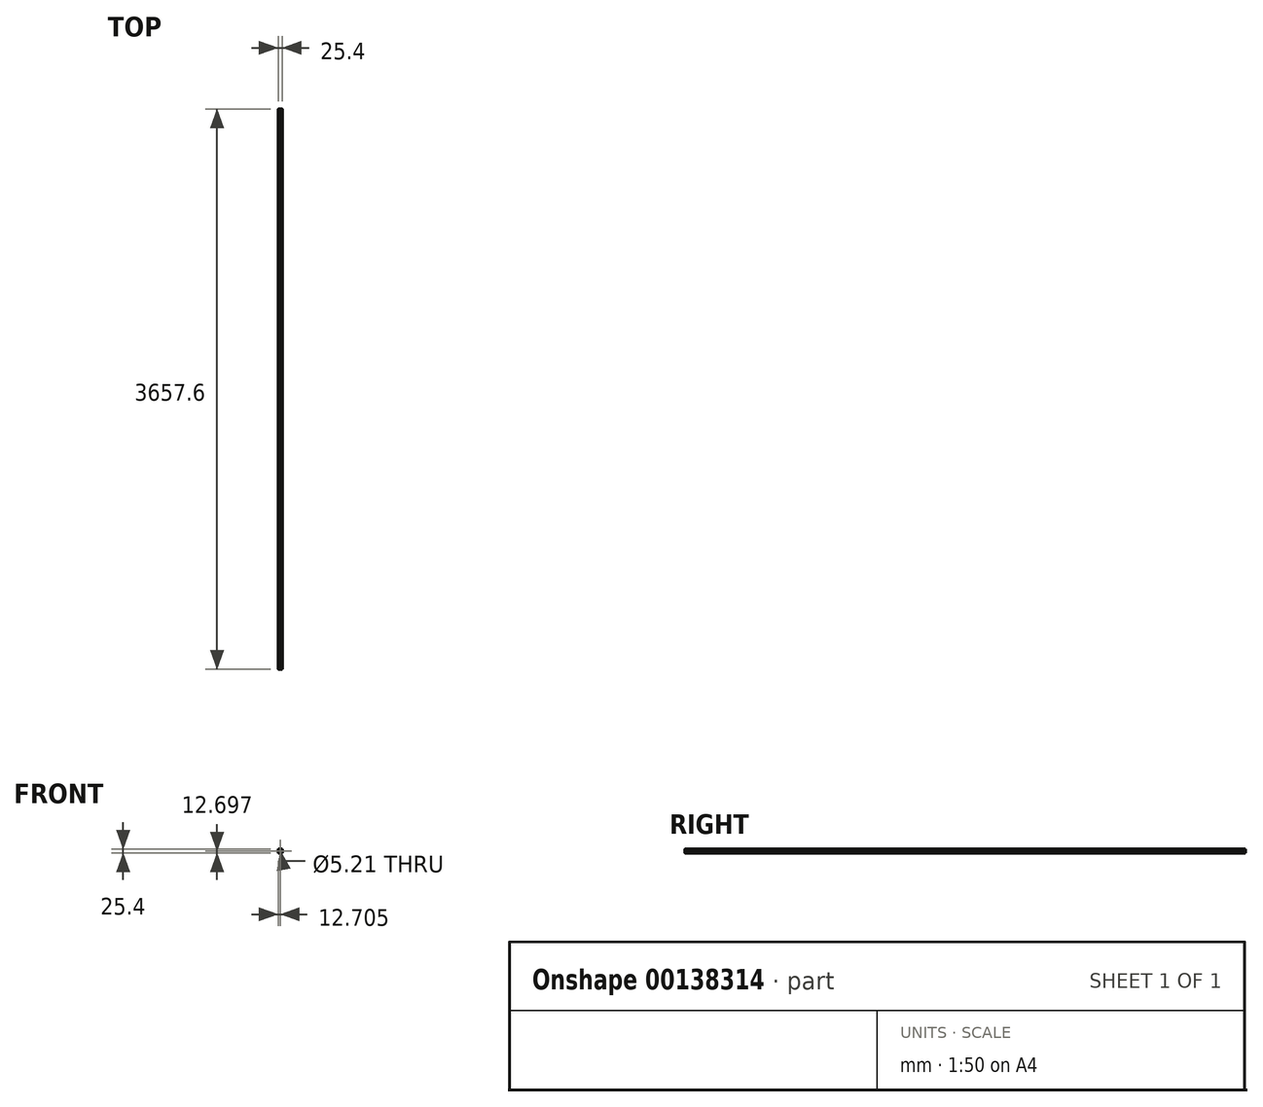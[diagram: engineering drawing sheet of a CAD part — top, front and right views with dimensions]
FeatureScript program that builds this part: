
annotation { "Feature Type Name" : "Feature", "Feature Type Description" : "" }
export const myFeature = defineFeature(function(context is Context, id is Id, definition is map)
    precondition{}
    {
        {
            var Q0;
            Q0=qCreatedBy(makeId("Front.planeOp"),FACE);
            var sketch = newSketch(context, id + "F0", { "sketchPlane" : qUnion([Q0])});
            skLineSegment(sketch, "E0.bottom", {"start": v(-12.7, 12.7) * mm, "end": v(12.7, 12.7) * mm});
            skLineSegment(sketch, "E0.top", {"start": v(-12.7, -12.7) * mm, "end": v(12.7, -12.7) * mm});
            skLineSegment(sketch, "E0.left", {"start": v(-12.7, 12.7) * mm, "end": v(-12.7, -12.7) * mm});
            skLineSegment(sketch, "E0.right", {"start": v(12.7, 12.7) * mm, "end": v(12.7, -12.7) * mm});
            skPoint(sketch, "E0.middle", {"position": v(0, 0) * mm});
            skLineSegment(sketch, "E1.bottom", {"start": v(-0.33, 4.52) * mm, "end": v(0.33, 4.52) * mm});
            skLineSegment(sketch, "E1.right", {"start": v(4.52, 3.37) * mm, "end": v(4.52, -2.64) * mm});
            skCircle(sketch, "E2", {"center": v(0, 0) * mm, "radius": 2.6 * mm});
            skLineSegment(sketch, "E3.0", {"start": v(-0.87, 4.74) * mm, "end": v(-7.97, 11.84) * mm});
            skLineSegment(sketch, "E4.0", {"start": v(-5.3, 3.74) * mm, "end": v(-13.48, 11.92) * mm});
            skLineSegment(sketch, "E5.MirrorCS", {"start": v(0.87, 4.74) * mm, "end": v(7.97, 11.84) * mm});
            skLineSegment(sketch, "E6.MirrorCS", {"start": v(5.3, 3.74) * mm, "end": v(13.48, 11.92) * mm});
            skLineSegment(sketch, "E7.MirrorCS", {"start": v(-4.64, 3.08) * mm, "end": v(-13.48, 11.92) * mm});
            skLineSegment(sketch, "E8.MirrorCS", {"start": v(-4.74, -3.18) * mm, "end": v(-13.48, -11.92) * mm});
            skLineSegment(sketch, "E9.MirrorCS", {"start": v(-5.3, -3.74) * mm, "end": v(-13.48, -11.92) * mm});
            skLineSegment(sketch, "E10.MirrorCS", {"start": v(-0.87, -4.74) * mm, "end": v(-7.97, -11.84) * mm});
            skLineSegment(sketch, "E11.MirrorCS", {"start": v(0.64, -4.52) * mm, "end": v(7.97, -11.84) * mm});
            skLineSegment(sketch, "E12.MirrorCS", {"start": v(0.87, -4.74) * mm, "end": v(7.97, -11.84) * mm});
            skLineSegment(sketch, "E13.MirrorCS", {"start": v(4.74, -3.18) * mm, "end": v(13.48, -11.92) * mm});
            skPoint(sketch, "E14.orphan", {"position": v(-5.3, 3.74) * mm});
            skPoint(sketch, "E15.orphan", {"position": v(-5.3, -3.74) * mm});
            skArc(sketch, "E16.filletArc", {"start": v(-0.33, -4.52) * mm, "mid": v(-0.62, -4.58) * mm, "end": v(-0.87, -4.74) * mm});
            skArc(sketch, "E17.filletArc", {"start": v(-4.74, -3.18) * mm, "mid": v(-4.58, -2.93) * mm, "end": v(-4.52, -2.64) * mm});
            skLineSegment(sketch, "E18", {"start": v(-4.52, -2.64) * mm, "end": v(-4.52, 2.41) * mm});
            skArc(sketch, "E19.filletArc", {"start": v(-0.87, 4.74) * mm, "mid": v(-0.62, 4.58) * mm, "end": v(-0.33, 4.52) * mm});
            skArc(sketch, "E20.filletArc", {"start": v(0.33, 4.52) * mm, "mid": v(0.62, 4.58) * mm, "end": v(0.87, 4.74) * mm});
            skArc(sketch, "E21.filletArc", {"start": v(4.52, -2.64) * mm, "mid": v(4.58, -2.93) * mm, "end": v(4.74, -3.18) * mm});
            skLineSegment(sketch, "E22", {"start": v(-0.33, -4.52) * mm, "end": v(0.33, -4.52) * mm});
            skPoint(sketch, "E23.visualSharp", {"position": v(0.64, -4.52) * mm});
            skArc(sketch, "E23.filletArc", {"start": v(0.87, -4.74) * mm, "mid": v(0.62, -4.58) * mm, "end": v(0.33, -4.52) * mm});
            skArc(sketch, "E24", {"start": v(-120.05, 65.1) * mm, "mid": v(-119.54, 65.6) * mm, "end": v(-120.05, 66.12) * mm});
            skLineSegment(sketch, "E25", {"start": v(-120.05, 69.33) * mm, "end": v(-120.05, 66.12) * mm});
            skArc(sketch, "E26", {"start": v(-120.05, 69.33) * mm, "mid": v(-119.54, 69.84) * mm, "end": v(-120.05, 70.35) * mm});
            skLineSegment(sketch, "E27", {"start": v(-120.05, 71.32) * mm, "end": v(-120.05, 70.35) * mm});
            skArc(sketch, "E28", {"start": v(-117.84, 71.32) * mm, "mid": v(-118.94, 72.43) * mm, "end": v(-120.05, 71.32) * mm});
            skLineSegment(sketch, "E29", {"start": v(-117.84, 69.2) * mm, "end": v(-117.84, 71.32) * mm});
            skArc(sketch, "E30", {"start": v(-117.84, 69.2) * mm, "mid": v(-117.2, 68.25) * mm, "end": v(-116.1, 68.47) * mm});
            skLineSegment(sketch, "E31", {"start": v(-112.77, 71.8) * mm, "end": v(-116.1, 68.47) * mm});
            skArc(sketch, "E32", {"start": v(-112.77, 71.8) * mm, "mid": v(-112.08, 72.83) * mm, "end": v(-111.84, 74.05) * mm});
            skLineSegment(sketch, "E33", {"start": v(-111.84, 77.28) * mm, "end": v(-111.84, 74.05) * mm});
            skArc(sketch, "E34", {"start": v(-111.84, 77.28) * mm, "mid": v(-112.08, 78.5) * mm, "end": v(-112.77, 79.53) * mm});
            skLineSegment(sketch, "E35", {"start": v(-116.1, 82.86) * mm, "end": v(-112.77, 79.53) * mm});
            skArc(sketch, "E36", {"start": v(-116.1, 82.86) * mm, "mid": v(-117.2, 83.08) * mm, "end": v(-117.84, 82.14) * mm});
            skLineSegment(sketch, "E37", {"start": v(-117.84, 80.01) * mm, "end": v(-117.84, 82.14) * mm});
            skArc(sketch, "E38", {"start": v(-120.05, 80.01) * mm, "mid": v(-118.94, 78.9) * mm, "end": v(-117.84, 80.01) * mm});
            skLineSegment(sketch, "E39", {"start": v(-120.05, 80.98) * mm, "end": v(-120.05, 80.01) * mm});
            skArc(sketch, "E40", {"start": v(-120.05, 80.98) * mm, "mid": v(-119.54, 81.5) * mm, "end": v(-120.05, 82) * mm});
            skLineSegment(sketch, "E41", {"start": v(-120.05, 85.22) * mm, "end": v(-120.05, 82) * mm});
            skArc(sketch, "E42", {"start": v(-120.05, 85.22) * mm, "mid": v(-119.54, 85.72) * mm, "end": v(-120.05, 86.23) * mm});
            skArc(sketch, "E43", {"start": v(-117.91, 88.37) * mm, "mid": v(-119.43, 87.75) * mm, "end": v(-120.05, 86.23) * mm});
            skArc(sketch, "E44", {"start": v(-117.91, 88.37) * mm, "mid": v(-117.4, 87.86) * mm, "end": v(-116.9, 88.37) * mm});
            skLineSegment(sketch, "E45", {"start": v(-113.68, 88.37) * mm, "end": v(-116.9, 88.37) * mm});
            skArc(sketch, "E46", {"start": v(-113.68, 88.37) * mm, "mid": v(-113.17, 87.86) * mm, "end": v(-112.66, 88.37) * mm});
            skLineSegment(sketch, "E47", {"start": v(-111.69, 88.37) * mm, "end": v(-112.66, 88.37) * mm});
            skArc(sketch, "E48", {"start": v(-111.69, 86.16) * mm, "mid": v(-110.58, 87.26) * mm, "end": v(-111.69, 88.37) * mm});
            skLineSegment(sketch, "E49", {"start": v(-113.82, 86.16) * mm, "end": v(-111.69, 86.16) * mm});
            skArc(sketch, "E50", {"start": v(-113.82, 86.16) * mm, "mid": v(-114.76, 85.53) * mm, "end": v(-114.54, 84.42) * mm});
            skLineSegment(sketch, "E51", {"start": v(-111.2, 81.1) * mm, "end": v(-114.54, 84.42) * mm});
            skArc(sketch, "E52", {"start": v(-111.2, 81.1) * mm, "mid": v(-110.18, 80.4) * mm, "end": v(-108.96, 80.16) * mm});
            skLineSegment(sketch, "E53", {"start": v(-105.73, 80.16) * mm, "end": v(-108.96, 80.16) * mm});
            skArc(sketch, "E54", {"start": v(-105.73, 80.16) * mm, "mid": v(-104.51, 80.4) * mm, "end": v(-103.48, 81.1) * mm});
            skLineSegment(sketch, "E55", {"start": v(-100.15, 84.42) * mm, "end": v(-103.48, 81.1) * mm});
            skArc(sketch, "E56", {"start": v(-100.15, 84.42) * mm, "mid": v(-99.93, 85.53) * mm, "end": v(-100.87, 86.16) * mm});
            skLineSegment(sketch, "E57", {"start": v(-103, 86.16) * mm, "end": v(-100.87, 86.16) * mm});
            skArc(sketch, "E58", {"start": v(-103, 88.37) * mm, "mid": v(-104.1, 87.26) * mm, "end": v(-103, 86.16) * mm});
            skLineSegment(sketch, "E59", {"start": v(-102.03, 88.37) * mm, "end": v(-103, 88.37) * mm});
            skArc(sketch, "E60", {"start": v(-102.03, 88.37) * mm, "mid": v(-101.52, 87.86) * mm, "end": v(-101.01, 88.37) * mm});
            skLineSegment(sketch, "E61", {"start": v(-97.8, 88.37) * mm, "end": v(-101.01, 88.37) * mm});
            skArc(sketch, "E62", {"start": v(-97.8, 88.37) * mm, "mid": v(-97.29, 87.86) * mm, "end": v(-96.78, 88.37) * mm});
            skArc(sketch, "E63", {"start": v(-94.65, 86.23) * mm, "mid": v(-95.26, 87.75) * mm, "end": v(-96.78, 88.37) * mm});
            skArc(sketch, "E64", {"start": v(-94.65, 86.23) * mm, "mid": v(-95.15, 85.72) * mm, "end": v(-94.65, 85.22) * mm});
            skLineSegment(sketch, "E65", {"start": v(-94.65, 82) * mm, "end": v(-94.65, 85.22) * mm});
            skArc(sketch, "E66", {"start": v(-94.65, 82) * mm, "mid": v(-95.15, 81.5) * mm, "end": v(-94.65, 80.98) * mm});
            skLineSegment(sketch, "E67", {"start": v(-94.65, 80.01) * mm, "end": v(-94.65, 80.98) * mm});
            skArc(sketch, "E68", {"start": v(-96.86, 80.01) * mm, "mid": v(-95.75, 78.9) * mm, "end": v(-94.65, 80.01) * mm});
            skLineSegment(sketch, "E69", {"start": v(-96.86, 82.14) * mm, "end": v(-96.86, 80.01) * mm});
            skArc(sketch, "E70", {"start": v(-96.86, 82.14) * mm, "mid": v(-97.48, 83.08) * mm, "end": v(-98.59, 82.86) * mm});
            skLineSegment(sketch, "E71", {"start": v(-101.92, 79.53) * mm, "end": v(-98.59, 82.86) * mm});
            skArc(sketch, "E72", {"start": v(-101.92, 79.53) * mm, "mid": v(-102.6, 78.5) * mm, "end": v(-102.85, 77.28) * mm});
            skLineSegment(sketch, "E73", {"start": v(-102.85, 74.05) * mm, "end": v(-102.85, 77.28) * mm});
            skArc(sketch, "E74", {"start": v(-102.85, 74.05) * mm, "mid": v(-102.6, 72.83) * mm, "end": v(-101.92, 71.8) * mm});
            skLineSegment(sketch, "E75", {"start": v(-98.59, 68.47) * mm, "end": v(-101.92, 71.8) * mm});
            skArc(sketch, "E76", {"start": v(-98.59, 68.47) * mm, "mid": v(-97.48, 68.25) * mm, "end": v(-96.86, 69.2) * mm});
            skLineSegment(sketch, "E77", {"start": v(-96.86, 71.32) * mm, "end": v(-96.86, 69.2) * mm});
            skArc(sketch, "E78", {"start": v(-94.65, 71.32) * mm, "mid": v(-95.75, 72.43) * mm, "end": v(-96.86, 71.32) * mm});
            skLineSegment(sketch, "E79", {"start": v(-94.65, 70.35) * mm, "end": v(-94.65, 71.32) * mm});
            skArc(sketch, "E80", {"start": v(-94.65, 70.35) * mm, "mid": v(-95.15, 69.84) * mm, "end": v(-94.65, 69.33) * mm});
            skLineSegment(sketch, "E81", {"start": v(-94.65, 66.12) * mm, "end": v(-94.65, 69.33) * mm});
            skArc(sketch, "E82", {"start": v(-94.65, 66.12) * mm, "mid": v(-95.15, 65.6) * mm, "end": v(-94.65, 65.1) * mm});
            skArc(sketch, "E83", {"start": v(-96.78, 62.97) * mm, "mid": v(-95.26, 63.58) * mm, "end": v(-94.65, 65.1) * mm});
            skArc(sketch, "E84", {"start": v(-96.78, 62.97) * mm, "mid": v(-97.29, 63.47) * mm, "end": v(-97.8, 62.97) * mm});
            skLineSegment(sketch, "E85", {"start": v(-101.01, 62.97) * mm, "end": v(-97.8, 62.97) * mm});
            skArc(sketch, "E86", {"start": v(-101.01, 62.97) * mm, "mid": v(-101.52, 63.47) * mm, "end": v(-102.03, 62.97) * mm});
            skLineSegment(sketch, "E87", {"start": v(-103, 62.97) * mm, "end": v(-102.03, 62.97) * mm});
            skArc(sketch, "E88", {"start": v(-103, 65.18) * mm, "mid": v(-104.1, 64.07) * mm, "end": v(-103, 62.97) * mm});
            skLineSegment(sketch, "E89", {"start": v(-100.87, 65.18) * mm, "end": v(-103, 65.18) * mm});
            skArc(sketch, "E90", {"start": v(-100.87, 65.18) * mm, "mid": v(-99.93, 65.8) * mm, "end": v(-100.15, 66.91) * mm});
            skLineSegment(sketch, "E91", {"start": v(-103.48, 70.24) * mm, "end": v(-100.15, 66.91) * mm});
            skArc(sketch, "E92", {"start": v(-103.48, 70.24) * mm, "mid": v(-104.51, 70.93) * mm, "end": v(-105.73, 71.17) * mm});
            skLineSegment(sketch, "E93", {"start": v(-108.96, 71.17) * mm, "end": v(-105.73, 71.17) * mm});
            skArc(sketch, "E94", {"start": v(-108.96, 71.17) * mm, "mid": v(-110.18, 70.93) * mm, "end": v(-111.2, 70.24) * mm});
            skLineSegment(sketch, "E95", {"start": v(-114.54, 66.91) * mm, "end": v(-111.2, 70.24) * mm});
            skArc(sketch, "E96", {"start": v(-114.54, 66.91) * mm, "mid": v(-114.76, 65.8) * mm, "end": v(-113.82, 65.18) * mm});
            skLineSegment(sketch, "E97", {"start": v(-111.69, 65.18) * mm, "end": v(-113.82, 65.18) * mm});
            skArc(sketch, "E98", {"start": v(-111.69, 62.97) * mm, "mid": v(-110.58, 64.07) * mm, "end": v(-111.69, 65.18) * mm});
            skLineSegment(sketch, "E99", {"start": v(-112.66, 62.97) * mm, "end": v(-111.69, 62.97) * mm});
            skArc(sketch, "E100", {"start": v(-112.66, 62.97) * mm, "mid": v(-113.17, 63.47) * mm, "end": v(-113.68, 62.97) * mm});
            skLineSegment(sketch, "E101", {"start": v(-116.9, 62.97) * mm, "end": v(-113.68, 62.97) * mm});
            skArc(sketch, "E102", {"start": v(-116.9, 62.97) * mm, "mid": v(-117.4, 63.47) * mm, "end": v(-117.91, 62.97) * mm});
            skArc(sketch, "E103", {"start": v(-120.05, 65.1) * mm, "mid": v(-119.43, 63.58) * mm, "end": v(-117.91, 62.97) * mm});
            skCircle(sketch, "E104", {"center": v(-107.35, 75.67) * mm, "radius": 2.6 * mm});
            skSolve(sketch);
        }
        {
            var Q0;
            Q0=makeQuery(id+"F0.imprint","IMPRINT",FACE,{"disambiguationData":[TD([[makeQuery(id+"F0.imprint","IMPRINT",EDGE,{"derivedFrom":sQuery(id+"F0.wireOp",EDGE,"E24")}),-1.0]])]});
            extrude(context, id + "F1", {"entities" : qUnion([Q0]), "endBound" : BoundingType.SYMMETRIC, "depth" : 3657.6 * mm});
        }
    });
